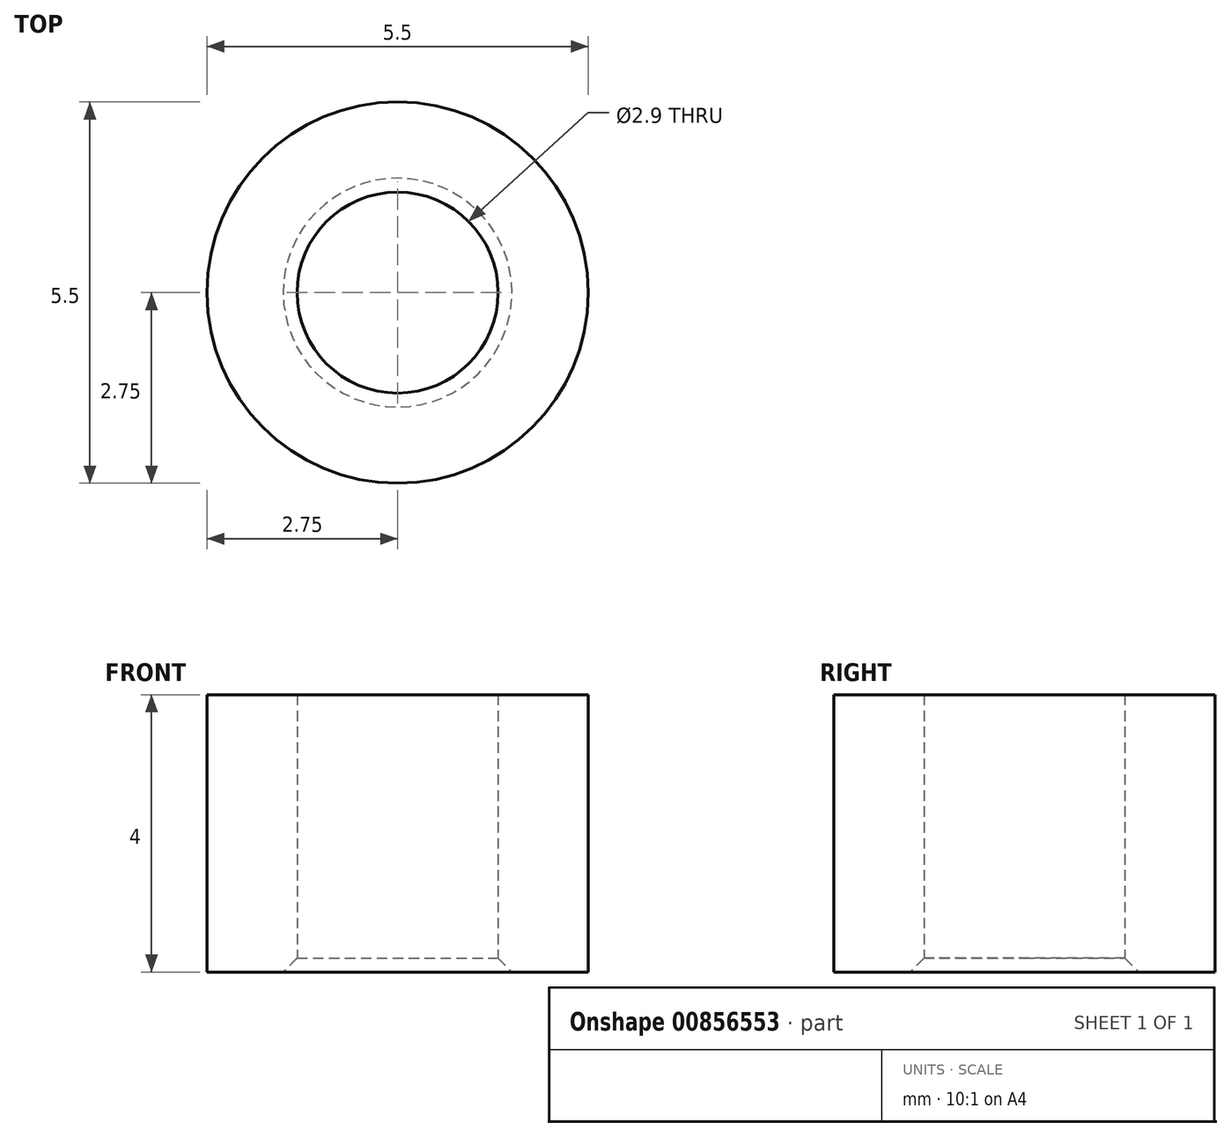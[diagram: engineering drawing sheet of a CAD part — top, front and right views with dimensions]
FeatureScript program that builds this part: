
annotation { "Feature Type Name" : "Feature", "Feature Type Description" : "" }
export const myFeature = defineFeature(function(context is Context, id is Id, definition is map)
    precondition{}
    {
        {
            var Q0;
            Q0=qCreatedBy(makeId("Front.planeOp"),FACE);
            var sketch = newSketch(context, id + "F0", { "sketchPlane" : qUnion([Q0])});
            skLineSegment(sketch, "E0.bottom", {"start": v(-1.45, 0) * mm, "end": v(-2.75, 0) * mm});
            skLineSegment(sketch, "E0.top", {"start": v(-1.45, 4) * mm, "end": v(-2.75, 4) * mm});
            skLineSegment(sketch, "E0.left", {"start": v(-1.45, 0) * mm, "end": v(-1.45, 4) * mm});
            skLineSegment(sketch, "E0.right", {"start": v(-2.75, 0) * mm, "end": v(-2.75, 4) * mm});
            skLineSegment(sketch, "E1", {"start": v(0, 0) * mm, "end": v(0, 8.75) * mm});
            skSolve(sketch);
        }
        {
            var Q0;
            Q0=makeQuery(id+"F0.imprint","IMPRINT",FACE,{"disambiguationData":[TD([[makeQuery(id+"F0.imprint","IMPRINT",EDGE,{"derivedFrom":sQuery(id+"F0.wireOp",EDGE,"E0.bottom")}),-1.0]])]});
            var Q1;
            Q1=sQuery(id+"F0.wireOp",EDGE,"E1");
            revolve(context, id + "F1", {"surfaceOperationType" : NewSurfaceOperationType.NEW, "entities" : qUnion([Q0]), "axis" : qUnion([Q1]), "revolveType" : RevolveType.FULL});
        }
        {
            var Q0;
            Q0=makeQuery(id+"F1.opRevolve","SWEPT_EDGE",EDGE,{"disambiguationData":[OSD([sQuery(id+"F0.wireOp",EDGE,"E0.bottom"),sQuery(id+"F0.wireOp",EDGE,"E0.left")])]});
            chamfer(context, id + "F2", {"entities" : qUnion([Q0]), "width" : 0.2 * mm});
        }
    });
